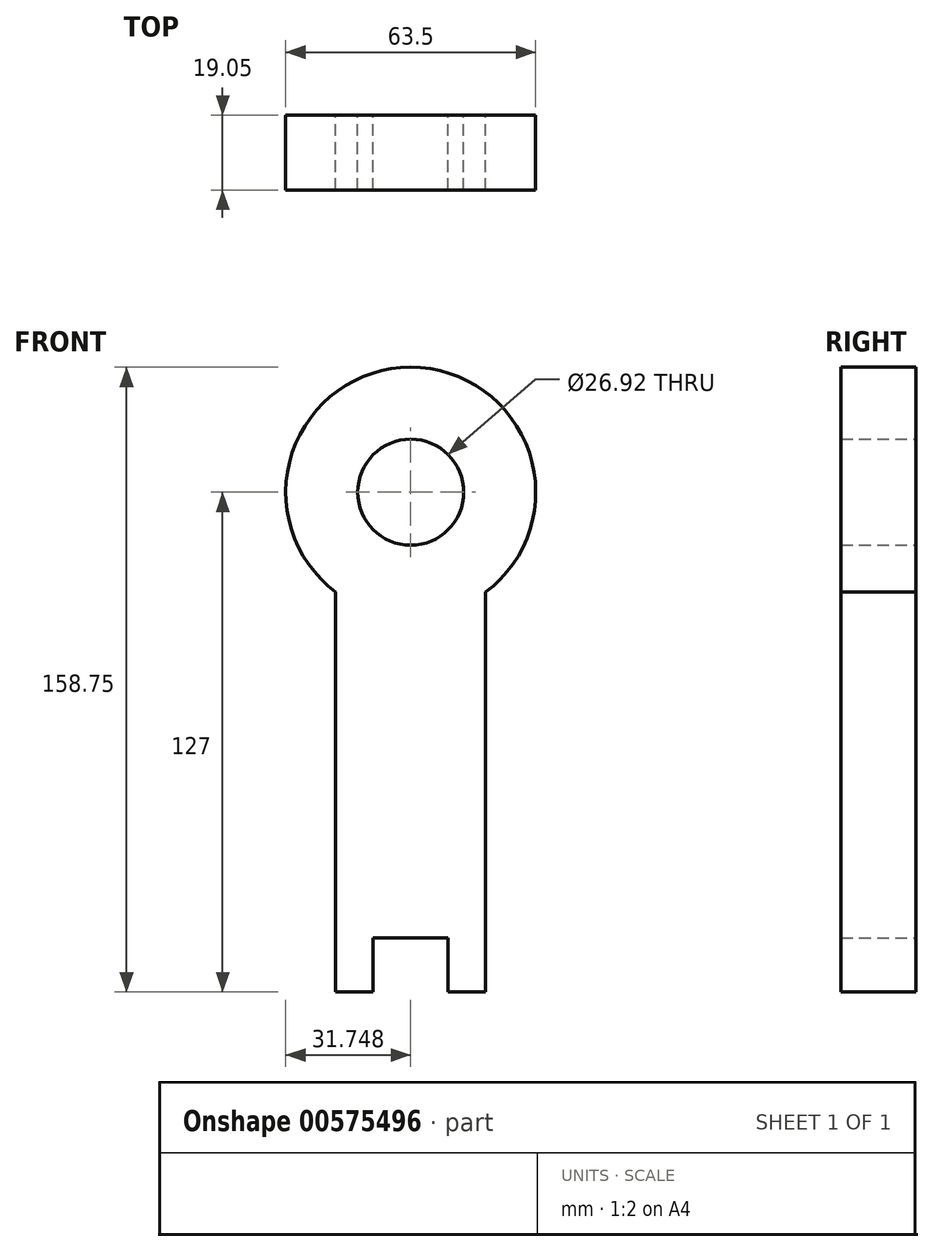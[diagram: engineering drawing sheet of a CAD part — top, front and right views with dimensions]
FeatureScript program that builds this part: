
annotation { "Feature Type Name" : "Feature", "Feature Type Description" : "" }
export const myFeature = defineFeature(function(context is Context, id is Id, definition is map)
    precondition{}
    {
        {
            var Q0;
            Q0=qCreatedBy(makeId("Front.planeOp"),FACE);
            var sketch = newSketch(context, id + "F0", { "sketchPlane" : qUnion([Q0])});
            skLineSegment(sketch, "E0.bottom", {"start": v(-52.16, -67.01) * mm, "end": v(-14.06, -67.01) * mm});
            skLineSegment(sketch, "E0.top", {"start": v(-52.16, 59.99) * mm, "end": v(-14.06, 59.99) * mm});
            skLineSegment(sketch, "E0.left", {"start": v(-52.16, -67.01) * mm, "end": v(-52.16, 59.99) * mm});
            skLineSegment(sketch, "E0.right", {"start": v(-14.06, -67.01) * mm, "end": v(-14.06, 59.99) * mm});
            skCircle(sketch, "E1", {"center": v(-33.11, 59.99) * mm, "radius": 13.46 * mm});
            skCircle(sketch, "E2", {"center": v(-33.11, 59.99) * mm, "radius": 31.75 * mm});
            skLineSegment(sketch, "E3.bottom", {"start": v(-23.59, -53.19) * mm, "end": v(-42.64, -53.19) * mm});
            skLineSegment(sketch, "E3.top", {"start": v(-23.59, -80.83) * mm, "end": v(-42.64, -80.83) * mm});
            skLineSegment(sketch, "E3.left", {"start": v(-23.59, -53.19) * mm, "end": v(-23.59, -80.83) * mm});
            skLineSegment(sketch, "E3.right", {"start": v(-42.64, -53.19) * mm, "end": v(-42.64, -80.83) * mm});
            skPoint(sketch, "E3.middle", {"position": v(-33.11, -67.01) * mm});
            skSolve(sketch);
        }
        {
            var Q0;
            {var subQ1=sQuery(id+"F0.wireOp",EDGE,"E0.top");var subQ5=sQuery(id+"F0.wireOp",EDGE,"E0.left");var subQ6=makeQuery(id+"F0.imprint","INTERSECT",VERTEX,{"derivedFrom":[subQ1,subQ5]});Q0=makeQuery(id+"F0.imprint","IMPRINT",FACE,{"disambiguationData":[TD([[makeQuery(id+"F0.imprint","IMPRINT",EDGE,{"disambiguationData":[TD([[subQ6,-1.0]])],"derivedFrom":subQ1}),1.0]])]});}
            var Q1;
            {var subQ1=sQuery(id+"F0.wireOp",EDGE,"E0.top");var subQ5=sQuery(id+"F0.wireOp",EDGE,"E0.left");var subQ6=makeQuery(id+"F0.imprint","INTERSECT",VERTEX,{"derivedFrom":[subQ1,subQ5]});Q1=makeQuery(id+"F0.imprint","IMPRINT",FACE,{"disambiguationData":[TD([[makeQuery(id+"F0.imprint","IMPRINT",EDGE,{"disambiguationData":[TD([[subQ6,-1.0]])],"derivedFrom":subQ1}),-1.0]])]});}
            var Q2;
            {var subQ0=sQuery(id+"F0.wireOp",EDGE,"E0.bottom");Q2=makeQuery(id+"F0.imprint","IMPRINT",FACE,{"disambiguationData":[TD([[makeQuery(id+"F0.imprint","IMPRINT",EDGE,{"derivedFrom":subQ0}),1.0]])]});}
            extrude(context, id + "F1", {"entities" : qUnion([Q0, Q1, Q2]), "depth" : 19.05 * mm, "offsetDistance" : 25.4 * mm});
        }
    });
